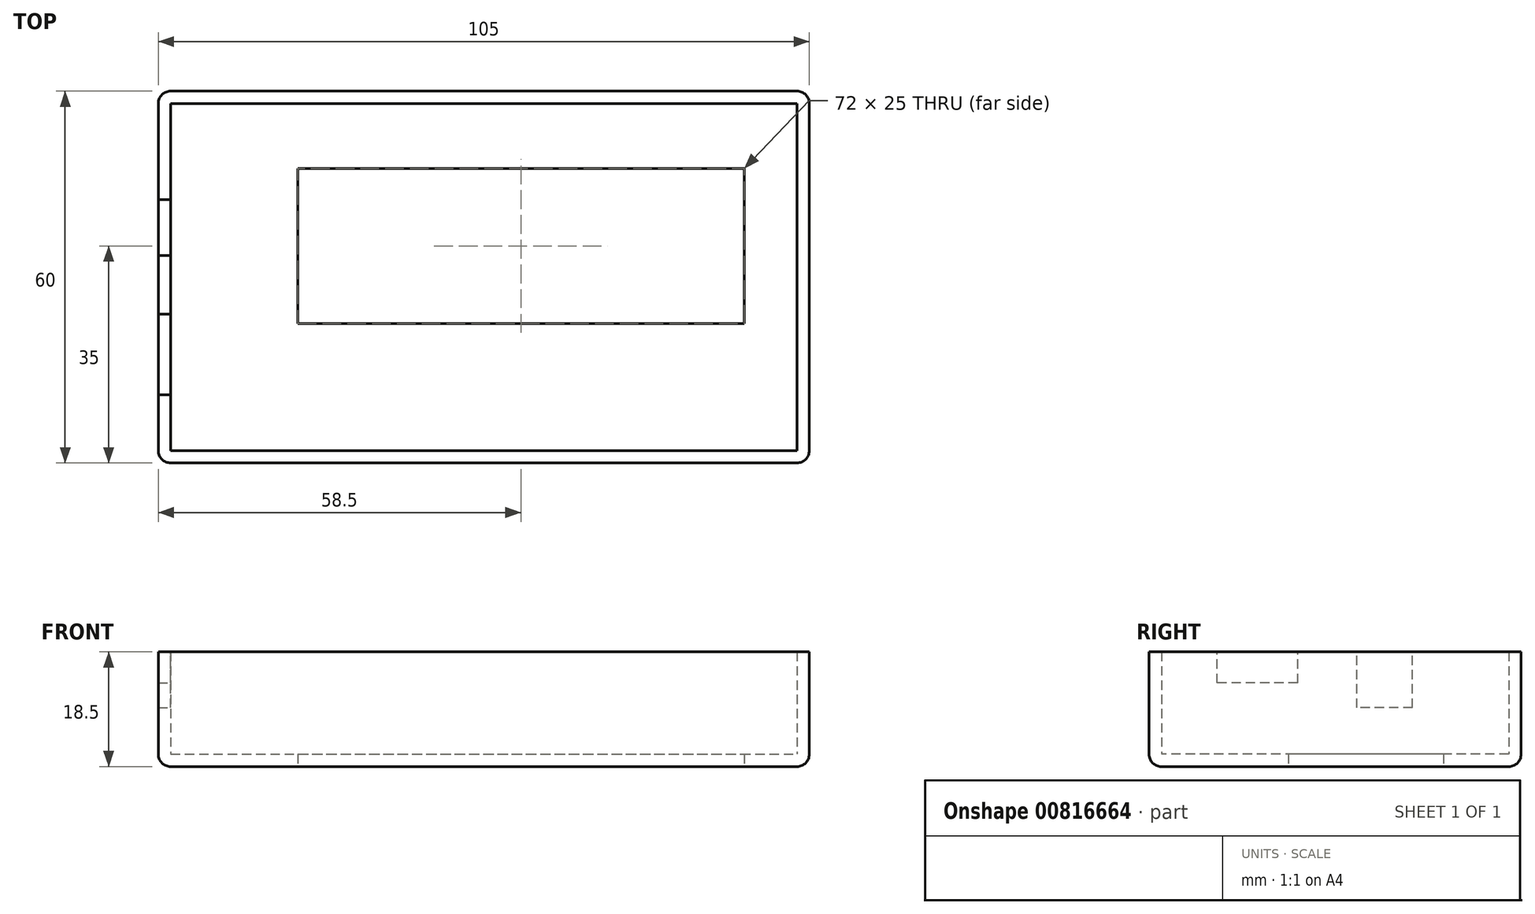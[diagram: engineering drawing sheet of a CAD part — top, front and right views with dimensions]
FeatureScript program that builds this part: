
annotation { "Feature Type Name" : "Feature", "Feature Type Description" : "" }
export const myFeature = defineFeature(function(context is Context, id is Id, definition is map)
    precondition{}
    {
        {
            var Q0;
            Q0=qCreatedBy(makeId("Top.planeOp"),FACE);
            var sketch = newSketch(context, id + "F0", { "sketchPlane" : qUnion([Q0])});
            skLineSegment(sketch, "E0.bottom", {"start": v(-52.5, 30) * mm, "end": v(52.5, 30) * mm});
            skLineSegment(sketch, "E0.top", {"start": v(-52.5, -30) * mm, "end": v(52.5, -30) * mm});
            skLineSegment(sketch, "E0.left", {"start": v(-52.5, 30) * mm, "end": v(-52.5, -30) * mm});
            skLineSegment(sketch, "E0.right", {"start": v(52.5, 30) * mm, "end": v(52.5, -30) * mm});
            skLineSegment(sketch, "E1.bottom", {"start": v(-30, 17.5) * mm, "end": v(42, 17.5) * mm});
            skLineSegment(sketch, "E1.top", {"start": v(-30, -7.5) * mm, "end": v(42, -7.5) * mm});
            skLineSegment(sketch, "E1.left", {"start": v(-30, 17.5) * mm, "end": v(-30, -7.5) * mm});
            skLineSegment(sketch, "E1.right", {"start": v(42, 17.5) * mm, "end": v(42, -7.5) * mm});
            skSolve(sketch);
        }
        {
            var Q0;
            Q0 = qSketchRegion(id + "F0", true);
            extrude(context, id + "F1", {"entities" : qUnion([Q0]), "depth" : 2 * mm, "offsetDistance" : 25 * mm});
        }
        {
            var Q0;
            Q0=makeQuery(id+"F1.opExtrude","CAP_FACE",FACE,{"disambiguationData":[OSD([sQuery(id+"F0.wireOp",EDGE,"E0.bottom"),sQuery(id+"F0.wireOp",EDGE,"E0.top"),sQuery(id+"F0.wireOp",EDGE,"E0.left"),sQuery(id+"F0.wireOp",EDGE,"E0.right")])],"isStart":false});
            var sketch = newSketch(context, id + "F2", { "sketchPlane" : qUnion([Q0])});
            skLineSegment(sketch, "E2.bottom", {"start": v(-52.5, -30) * mm, "end": v(52.5, -30) * mm});
            skLineSegment(sketch, "E2.top", {"start": v(-52.5, 30) * mm, "end": v(52.5, 30) * mm});
            skLineSegment(sketch, "E2.left", {"start": v(-52.5, -30) * mm, "end": v(-52.5, 30) * mm});
            skLineSegment(sketch, "E2.right", {"start": v(52.5, -30) * mm, "end": v(52.5, 30) * mm});
            skLineSegment(sketch, "E3.bottom", {"start": v(-50.5, 28) * mm, "end": v(50.5, 28) * mm});
            skLineSegment(sketch, "E3.top", {"start": v(-50.5, -28) * mm, "end": v(50.5, -28) * mm});
            skLineSegment(sketch, "E3.left", {"start": v(-50.5, 28) * mm, "end": v(-50.5, -28) * mm});
            skLineSegment(sketch, "E3.right", {"start": v(50.5, 28) * mm, "end": v(50.5, -28) * mm});
            skSolve(sketch);
        }
        {
            var Q0;
            Q0 = qSketchRegion(id + "F2", true);
            extrude(context, id + "F3", {"entities" : qUnion([Q0]), "operationType" : NewBodyOperationType.ADD, "depth" : 16.5 * mm, "offsetDistance" : 25 * mm});
        }
        {
            var Q0;
            Q0=makeQuery(id+"F3.opExtrude","CAP_FACE",FACE,{"disambiguationData":[OSD([sQuery(id+"F2.wireOp",EDGE,"E2.bottom"),sQuery(id+"F2.wireOp",EDGE,"E2.top"),sQuery(id+"F2.wireOp",EDGE,"E2.left"),sQuery(id+"F2.wireOp",EDGE,"E2.right"),sQuery(id+"F2.wireOp",EDGE,"E3.bottom"),sQuery(id+"F2.wireOp",EDGE,"E3.top"),sQuery(id+"F2.wireOp",EDGE,"E3.left"),sQuery(id+"F2.wireOp",EDGE,"E3.right")])],"isStart":false});
            var sketch = newSketch(context, id + "F4", { "sketchPlane" : qUnion([Q0])});
            skLineSegment(sketch, "E4.bottom", {"start": v(-52.5, 12.5) * mm, "end": v(-50.5, 12.5) * mm});
            skLineSegment(sketch, "E4.top", {"start": v(-52.5, 3.5) * mm, "end": v(-50.5, 3.5) * mm});
            skLineSegment(sketch, "E4.left", {"start": v(-52.5, 12.5) * mm, "end": v(-52.5, 3.5) * mm});
            skLineSegment(sketch, "E4.right", {"start": v(-50.5, 12.5) * mm, "end": v(-50.5, 3.5) * mm});
            skLineSegment(sketch, "E5.bottom", {"start": v(-52.5, -6) * mm, "end": v(-50.5, -6) * mm});
            skLineSegment(sketch, "E5.top", {"start": v(-52.5, -19) * mm, "end": v(-50.5, -19) * mm});
            skLineSegment(sketch, "E5.left", {"start": v(-52.5, -6) * mm, "end": v(-52.5, -19) * mm});
            skLineSegment(sketch, "E5.right", {"start": v(-50.5, -6) * mm, "end": v(-50.5, -19) * mm});
            skSolve(sketch);
        }
        {
            var Q0;
            Q0 = qSketchRegion(id + "F4", true);
            extrude(context, id + "F5", {"entities" : qUnion([Q0]), "operationType" : NewBodyOperationType.REMOVE, "oppositeDirection" : true, "depth" : 9 * mm, "offsetDistance" : 25 * mm});
        }
        {
            var Q0;
            Q0=makeQuery(id+"F3.boolean.opBoolean","MERGE",EDGE,{"derivedFrom":[makeQuery(id+"F1.opExtrude","SWEPT_EDGE",EDGE,{"disambiguationData":[OSD([sQuery(id+"F0.wireOp",EDGE,"E0.top"),sQuery(id+"F0.wireOp",EDGE,"E0.right")])]}),makeQuery(id+"F3.opExtrude","SWEPT_EDGE",EDGE,{"disambiguationData":[OSD([sQuery(id+"F2.wireOp",EDGE,"E2.bottom"),sQuery(id+"F2.wireOp",EDGE,"E2.right")])]})]});
            var Q1;
            Q1=makeQuery(id+"F3.boolean.opBoolean","MERGE",EDGE,{"derivedFrom":[makeQuery(id+"F1.opExtrude","SWEPT_EDGE",EDGE,{"disambiguationData":[OSD([sQuery(id+"F0.wireOp",EDGE,"E0.bottom"),sQuery(id+"F0.wireOp",EDGE,"E0.right")])]}),makeQuery(id+"F3.opExtrude","SWEPT_EDGE",EDGE,{"disambiguationData":[OSD([sQuery(id+"F2.wireOp",EDGE,"E2.top"),sQuery(id+"F2.wireOp",EDGE,"E2.right")])]})]});
            var Q2;
            Q2=makeQuery(id+"F3.boolean.opBoolean","MERGE",EDGE,{"derivedFrom":[makeQuery(id+"F1.opExtrude","SWEPT_EDGE",EDGE,{"disambiguationData":[OSD([sQuery(id+"F0.wireOp",EDGE,"E0.top"),sQuery(id+"F0.wireOp",EDGE,"E0.left")])]}),makeQuery(id+"F3.opExtrude","SWEPT_EDGE",EDGE,{"disambiguationData":[OSD([sQuery(id+"F2.wireOp",EDGE,"E2.bottom"),sQuery(id+"F2.wireOp",EDGE,"E2.left")])]})]});
            var Q3;
            Q3=makeQuery(id+"F3.boolean.opBoolean","MERGE",EDGE,{"derivedFrom":[makeQuery(id+"F1.opExtrude","SWEPT_EDGE",EDGE,{"disambiguationData":[OSD([sQuery(id+"F0.wireOp",EDGE,"E0.bottom"),sQuery(id+"F0.wireOp",EDGE,"E0.left")])]}),makeQuery(id+"F3.opExtrude","SWEPT_EDGE",EDGE,{"disambiguationData":[OSD([sQuery(id+"F2.wireOp",EDGE,"E2.top"),sQuery(id+"F2.wireOp",EDGE,"E2.left")])]})]});
            fillet(context, id + "F6", {"entities" : qUnion([Q0, Q1, Q2, Q3]), "radius" : 2 * mm, "tangentPropagation" : true, "allowEdgeOverflow" : false});
        }
        {
            var Q0;
            Q0=makeQuery(id+"F1.opExtrude","CAP_EDGE",EDGE,{"disambiguationData":[OSD([sQuery(id+"F0.wireOp",EDGE,"E0.right")])],"isStart":true});
            var Q1;
            Q1=makeQuery(id+"F1.opExtrude","CAP_EDGE",EDGE,{"disambiguationData":[OSD([sQuery(id+"F0.wireOp",EDGE,"E0.top")])],"isStart":true});
            var Q2;
            Q2=makeQuery(id+"F1.opExtrude","CAP_EDGE",EDGE,{"disambiguationData":[OSD([sQuery(id+"F0.wireOp",EDGE,"E0.bottom")])],"isStart":true});
            var Q3;
            Q3=makeQuery(id+"F1.opExtrude","CAP_EDGE",EDGE,{"disambiguationData":[OSD([sQuery(id+"F0.wireOp",EDGE,"E0.left")])],"isStart":true});
            fillet(context, id + "F7", {"entities" : qUnion([Q0, Q1, Q2, Q3]), "radius" : 2 * mm, "tangentPropagation" : true, "allowEdgeOverflow" : false});
        }
        {
            var Q0;
            Q0=makeQuery(id+"F5.boolean.opBoolean","COPY",FACE,{"derivedFrom":makeQuery(id+"F5.opExtrude","CAP_FACE",FACE,{"disambiguationData":[OSD([sQuery(id+"F4.wireOp",EDGE,"E5.bottom"),sQuery(id+"F4.wireOp",EDGE,"E5.top"),sQuery(id+"F4.wireOp",EDGE,"E5.left"),sQuery(id+"F4.wireOp",EDGE,"E5.right")])],"isStart":false})});
            var sketch = newSketch(context, id + "F8", { "sketchPlane" : qUnion([Q0])});
            skLineSegment(sketch, "E6.bottom", {"start": v(-52.5, -6) * mm, "end": v(-50.5, -6) * mm});
            skLineSegment(sketch, "E6.top", {"start": v(-52.5, -19) * mm, "end": v(-50.5, -19) * mm});
            skLineSegment(sketch, "E6.left", {"start": v(-52.5, -6) * mm, "end": v(-52.5, -19) * mm});
            skLineSegment(sketch, "E6.right", {"start": v(-50.5, -6) * mm, "end": v(-50.5, -19) * mm});
            skSolve(sketch);
        }
        {
            var Q0;
            Q0 = qSketchRegion(id + "F8", true);
            extrude(context, id + "F9", {"entities" : qUnion([Q0]), "operationType" : NewBodyOperationType.ADD, "depth" : 4 * mm, "offsetDistance" : 25 * mm});
        }
    });
